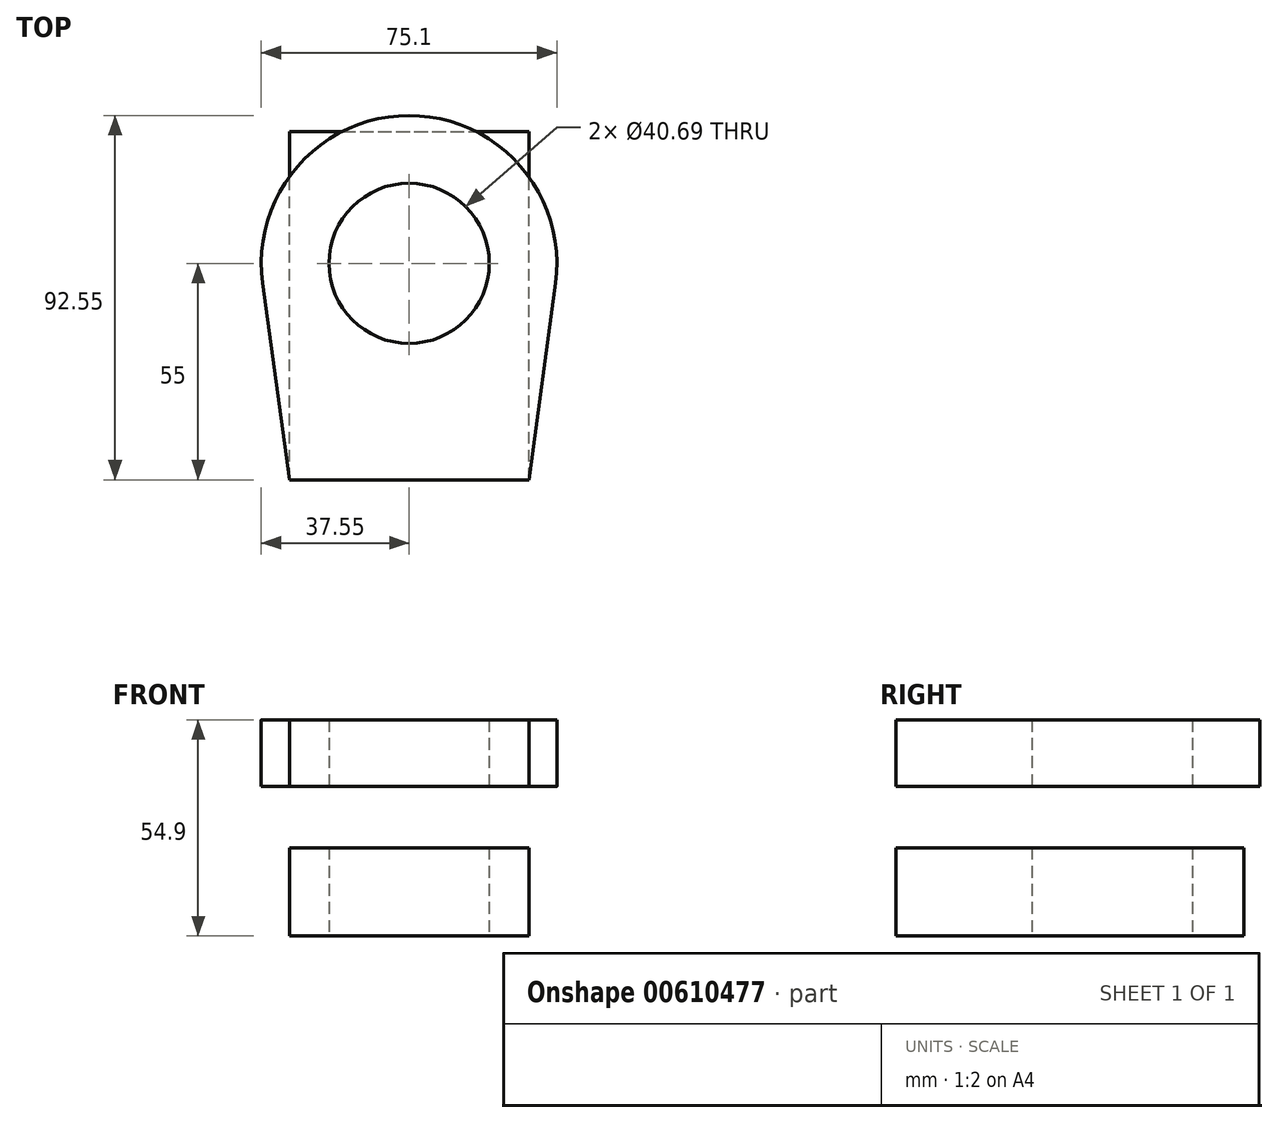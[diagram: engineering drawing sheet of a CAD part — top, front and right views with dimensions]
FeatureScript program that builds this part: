
annotation { "Feature Type Name" : "Feature", "Feature Type Description" : "" }
export const myFeature = defineFeature(function(context is Context, id is Id, definition is map)
    precondition{}
    {
        {
            var Q0;
            Q0=qCreatedBy(makeId("Top.planeOp"),FACE);
            var sketch = newSketch(context, id + "F0", { "sketchPlane" : qUnion([Q0])});
            skCircle(sketch, "E0", {"center": v(0, 0) * mm, "radius": 20.35 * mm});
            skLineSegment(sketch, "E1", {"start": v(-30.42, -55) * mm, "end": v(30.42, -55) * mm});
            skLineSegment(sketch, "E2.left", {"start": v(30.42, -55) * mm, "end": v(30.42, 33.42) * mm});
            skLineSegment(sketch, "E2.right", {"start": v(-30.42, -55) * mm, "end": v(-30.42, 33.42) * mm});
            skLineSegment(sketch, "E3", {"start": v(-30.42, 33.42) * mm, "end": v(30.42, 33.42) * mm});
            skPoint(sketch, "E4.orphan", {"position": v(-30.42, 86.17) * mm});
            skPoint(sketch, "E5.orphan", {"position": v(30.42, 86.17) * mm});
            skPoint(sketch, "E2.bottom.start.orphan", {"position": v(30.42, -86.17) * mm});
            skPoint(sketch, "E6.orphan", {"position": v(-30.42, -86.17) * mm});
            skSolve(sketch);
        }
        {
            var Q0;
            Q0=makeQuery(id+"F0.imprint","IMPRINT",FACE,{"disambiguationData":[TD([[makeQuery(id+"F0.imprint","IMPRINT",EDGE,{"derivedFrom":sQuery(id+"F0.wireOp",EDGE,"E0")}),-1.0]])]});
            extrude(context, id + "F1", {"entities" : qUnion([Q0]), "depth" : 22.4 * mm, "offsetDistance" : 25 * mm});
        }
        {
            var Q0;
            Q0=qCreatedBy(makeId("Top.planeOp"),FACE);
            var sketch = newSketch(context, id + "F2", { "sketchPlane" : qUnion([Q0])});
            skCircle(sketch, "E7.0", {"center": v(0, 0) * mm, "radius": 20.35 * mm});
            skCircle(sketch, "E8.0", {"center": v(0, 0) * mm, "radius": 37.55 * mm});
            skLineSegment(sketch, "E9.0", {"start": v(-30.42, -55) * mm, "end": v(30.42, -55) * mm});
            skLineSegment(sketch, "E10", {"start": v(30.42, -55) * mm, "end": v(37.2, -5.05) * mm});
            skLineSegment(sketch, "E11", {"start": v(-30.42, -55) * mm, "end": v(-37.2, -5.05) * mm});
            skSolve(sketch);
        }
        {
            var Q0;
            Q0=makeQuery(id+"F2.imprint","IMPRINT",FACE,{"disambiguationData":[TD([[makeQuery(id+"F2.imprint","IMPRINT",EDGE,{"derivedFrom":sQuery(id+"F2.wireOp",EDGE,"E7.0")}),-1.0]])]});
            var Q1;
            Q1=makeQuery(id+"F2.imprint","IMPRINT",FACE,{"disambiguationData":[TD([[makeQuery(id+"F2.imprint","IMPRINT",EDGE,{"derivedFrom":sQuery(id+"F2.wireOp",EDGE,"E9.0")}),1.0]])]});
            extrude(context, id + "F3", {"entities" : qUnion([Q0, Q1]), "depth" : 54.9 * mm, "offsetDistance" : 25 * mm, "hasSecondDirection" : true, "secondDirectionOppositeDirection" : false, "secondDirectionDepth" : 38 * mm});
        }
    });
